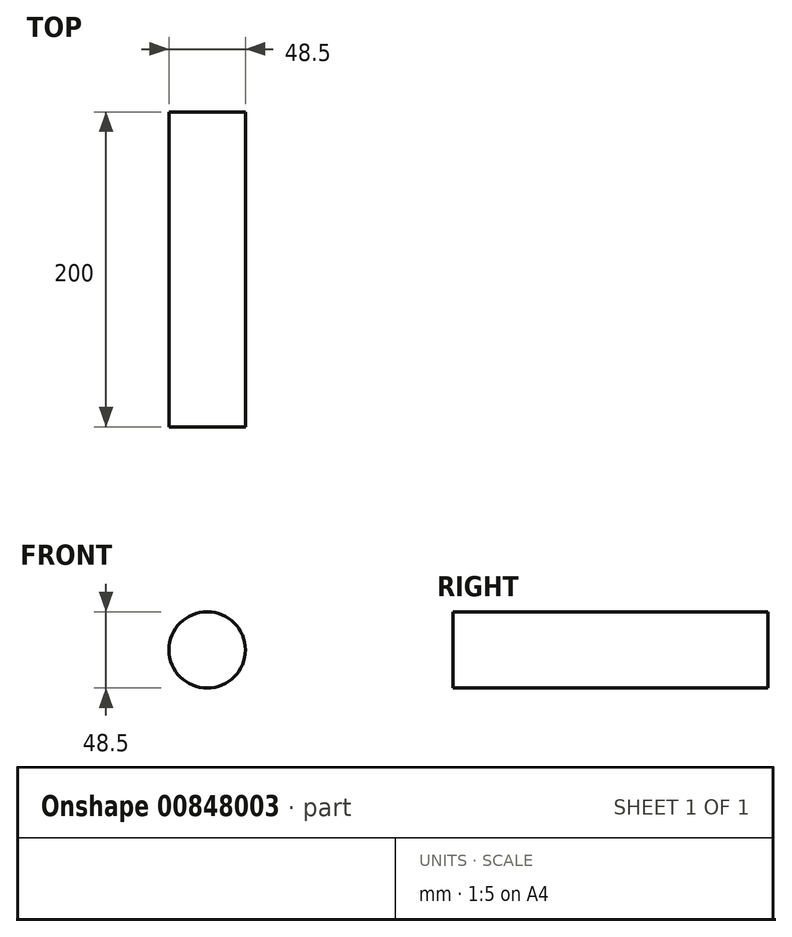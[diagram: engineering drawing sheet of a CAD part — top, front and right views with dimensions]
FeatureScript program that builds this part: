
annotation { "Feature Type Name" : "Feature", "Feature Type Description" : "" }
export const myFeature = defineFeature(function(context is Context, id is Id, definition is map)
    precondition{}
    {
        {
            var Q0;
            Q0=qCreatedBy(makeId("Front.planeOp"),FACE);
            var sketch = newSketch(context, id + "F0", { "sketchPlane" : qUnion([Q0])});
            skCircle(sketch, "E0", {"center": v(0, 0) * mm, "radius": 24.25 * mm});
            skSolve(sketch);
        }
        {
            var Q0;
            Q0 = qSketchRegion(id + "F0", true);
            extrude(context, id + "F1", {"entities" : qUnion([Q0]), "depth" : 200 * mm, "offsetDistance" : 25 * mm});
        }
    });
